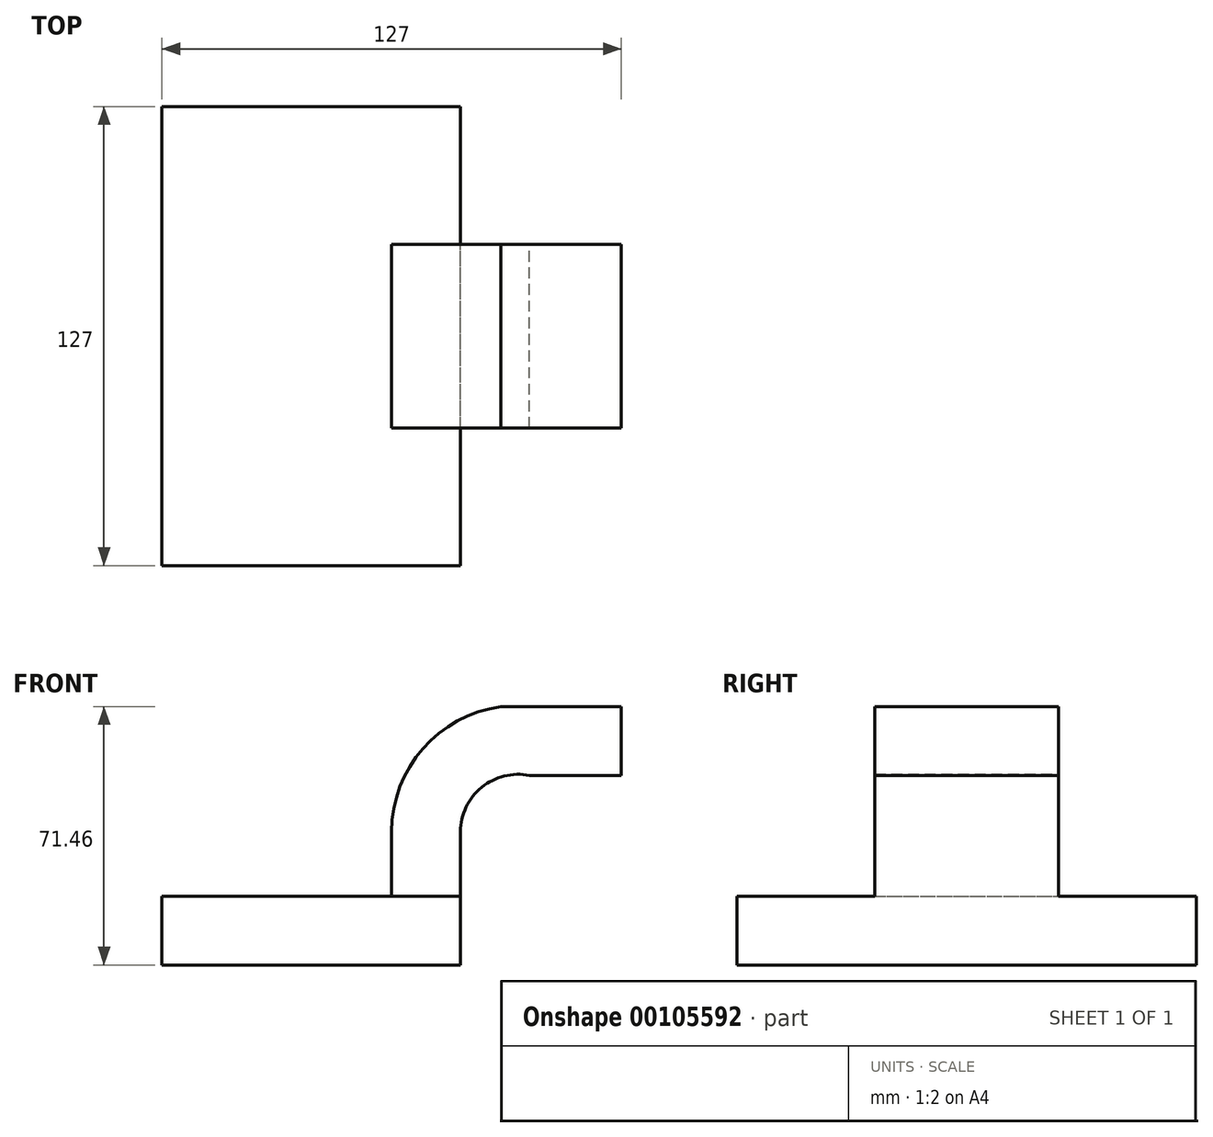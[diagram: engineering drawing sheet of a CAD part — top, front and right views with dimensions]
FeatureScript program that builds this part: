
annotation { "Feature Type Name" : "Feature", "Feature Type Description" : "" }
export const myFeature = defineFeature(function(context is Context, id is Id, definition is map)
    precondition{}
    {
        {
            var Q0;
            Q0=qCreatedBy(makeId("Front.planeOp"),FACE);
            var sketch = newSketch(context, id + "F0", { "sketchPlane" : qUnion([Q0])});
            skLineSegment(sketch, "E0.bottom", {"start": v(41.28, 9.53) * mm, "end": v(-41.28, 9.53) * mm});
            skLineSegment(sketch, "E0.top", {"start": v(41.28, -9.52) * mm, "end": v(-41.28, -9.53) * mm});
            skLineSegment(sketch, "E0.left", {"start": v(41.28, 9.53) * mm, "end": v(41.28, -9.52) * mm});
            skLineSegment(sketch, "E0.right", {"start": v(-41.28, 9.53) * mm, "end": v(-41.28, -9.53) * mm});
            skPoint(sketch, "E0.middle", {"position": v(0, 0) * mm});
            skLineSegment(sketch, "E1", {"start": v(41.28, 9.53) * mm, "end": v(41.28, 27.32) * mm});
            skArc(sketch, "E2", {"start": v(41.27, 27.32) * mm, "mid": v(47.1, 39.62) * mm, "end": v(60.32, 42.88) * mm});
            skLineSegment(sketch, "E3.bottom", {"start": v(60.33, 38.1) * mm, "end": v(111.13, 38.1) * mm});
            skLineSegment(sketch, "E3.top", {"start": v(60.33, 66.68) * mm, "end": v(111.13, 66.68) * mm});
            skLineSegment(sketch, "E3.left", {"start": v(60.33, 38.1) * mm, "end": v(60.33, 66.68) * mm});
            skLineSegment(sketch, "E3.right", {"start": v(111.13, 38.1) * mm, "end": v(111.13, 66.68) * mm});
            skLineSegment(sketch, "E4", {"start": v(60.32, 42.88) * mm, "end": v(85.72, 42.88) * mm});
            skLineSegment(sketch, "E5.0", {"start": v(52.43, 61.93) * mm, "end": v(85.77, 61.93) * mm});
            skArc(sketch, "E5.1", {"start": v(22.22, 27.32) * mm, "mid": v(30.84, 50.29) * mm, "end": v(52.43, 61.93) * mm});
            skLineSegment(sketch, "E5.2", {"start": v(22.22, 9.53) * mm, "end": v(22.22, 27.32) * mm});
            skFitSpline(sketch, "E6", {"points": [v(-41.28, 9.52) * mm, v(52.43, 61.93) * mm], "startDerivative": vector(-0.65, 112.48) * mm, "endDerivative": vector(113.24, 1.85) * mm});
            skLineSegment(sketch, "E7", {"start": v(60.33, 38.1) * mm, "end": v(111.13, 66.68) * mm, "construction": true});
            skLineSegment(sketch, "E8", {"start": v(85.72, 52.39) * mm, "end": v(85.72, 42.88) * mm, "construction": true});
            skLineSegment(sketch, "E9", {"start": v(85.73, 38.1) * mm, "end": v(85.73, 66.68) * mm});
            skSolve(sketch);
        }
        {
            var Q0;
            Q0=makeQuery(id+"F0.imprint","IMPRINT",FACE,{"disambiguationData":[TD([[makeQuery(id+"F0.imprint","IMPRINT",EDGE,{"derivedFrom":sQuery(id+"F0.wireOp",EDGE,"E0.top")}),-1.0]])]});
            extrude(context, id + "F1", {"entities" : qUnion([Q0]), "endBound" : BoundingType.SYMMETRIC, "depth" : 127 * mm});
        }
        {
            var Q0;
            {var subQ4=sQuery(id+"F0.wireOp",EDGE,"E1");Q0=makeQuery(id+"F0.imprint","IMPRINT",FACE,{"disambiguationData":[TD([[makeQuery(id+"F0.imprint","IMPRINT",EDGE,{"derivedFrom":subQ4}),1.0]])]});}
            var Q1;
            {var subQ0=sQuery(id+"F0.wireOp",EDGE,"E4");Q1=makeQuery(id+"F0.imprint","IMPRINT",FACE,{"disambiguationData":[TD([[makeQuery(id+"F0.imprint","IMPRINT",EDGE,{"derivedFrom":subQ0}),1.0]])]});}
            extrude(context, id + "F2", {"entities" : qUnion([Q0, Q1]), "operationType" : NewBodyOperationType.ADD, "endBound" : BoundingType.SYMMETRIC, "depth" : 50.8 * mm});
        }
        {
            var Q0;
            Q0=makeQuery(id+"F0.imprint","IMPRINT",FACE,{"disambiguationData":[TD([[makeQuery(id+"F0.imprint","IMPRINT",EDGE,{"derivedFrom":sQuery(id+"F0.wireOp",EDGE,"E5.1")}),1.0]])]});
            extrude(context, id + "F3", {"entities" : qUnion([Q0]), "operationType" : NewBodyOperationType.ADD, "endBound" : BoundingType.SYMMETRIC, "depth" : 15.88 * mm});
        }
    });
